# Revit family: AROHA - Lavabo alto TERM
name_source: partatom
category: Aparatos sanitarios
revit_build: Autodesk Revit 2016 (Build: 20150220_1215(x64)
units: mm (PartAtom-declared; Revit-internal decimal feet)

## family parameters
Anfitrión = Cara
Compartido = No
Corte con vacíos al cargar = No
Cota de conector redondo = Diámetro de uso
Número OmniClass = 23.45.05.14.14
Punto de cálculo de habitación = No
Tipo de pieza = Normal
Título OmniClass = Sinks/Lavatories

## types (1)
- AROHA - Lavabo alto TERM
    Accionamiento = Por maneta
    CWFU = 1
    Caudal = 6.0 L/min
    Cierre = Manual
    Comentarios de tipo = Cartucho sellado mezclador con discos cerámicos de diámetro 35 mm.
    Código de montaje = D2020
    Descripción = Grifería de cuello largo para lavabo.
    Diámetro entrada = 1"
    Elevación por defecto = 48"
    Fabricante = GALINDO
    HWFU = 1
    Material = Latón, cromado
    Modelo = AROHA Lavabo alto
    Notas de suministro = Suministrados con latiguillos flexibles hembra de 1/2” y longitud 60 cm.
    Referencia = 4605500
    Sistema = AFS / ACS
    Teléfono = +34 93 680 13 15
    URL = http://www.griferiasgalindo.com
    WFU = 0
